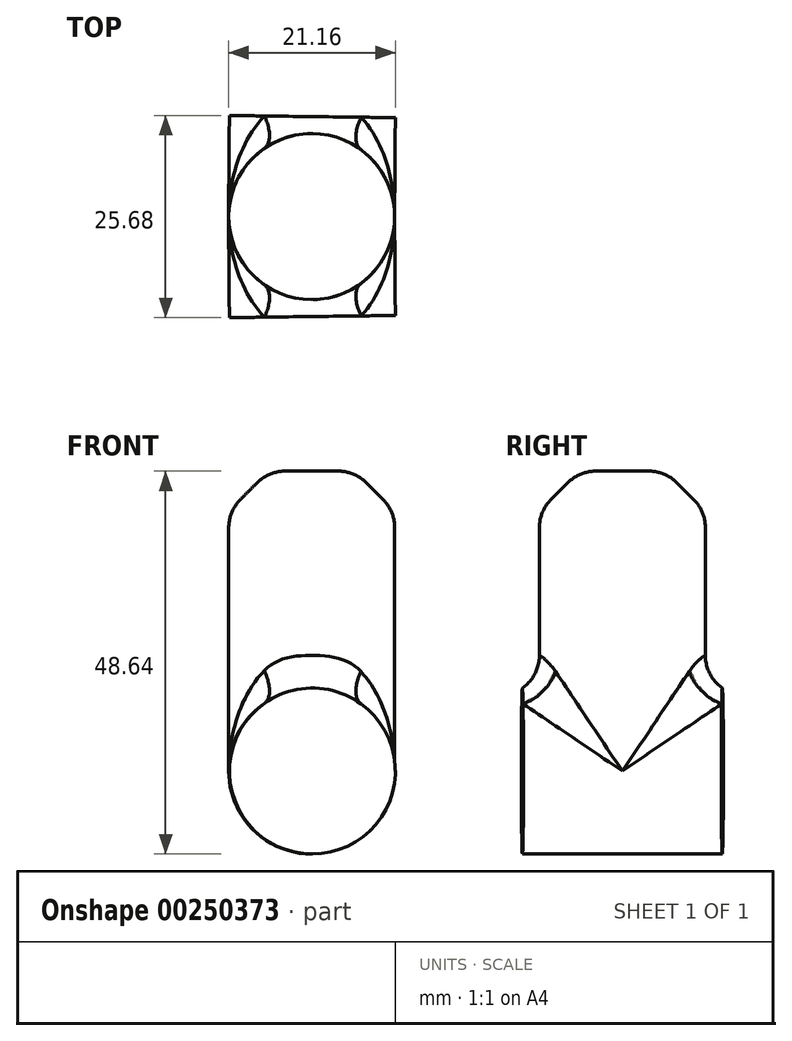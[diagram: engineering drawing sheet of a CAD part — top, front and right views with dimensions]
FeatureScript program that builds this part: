
annotation { "Feature Type Name" : "Feature", "Feature Type Description" : "" }
export const myFeature = defineFeature(function(context is Context, id is Id, definition is map)
    precondition{}
    {
        {
            var Q0;
            Q0=qCreatedBy(makeId("Front.planeOp"),FACE);
            var sketch = newSketch(context, id + "F0", { "sketchPlane" : qUnion([Q0])});
            skCircle(sketch, "E0", {"center": v(0, 0) * mm, "radius": 7.62 * mm});
            skSolve(sketch);
        }
        {
            var Q0;
            Q0=qCreatedBy(makeId("Top.planeOp"),FACE);
            var sketch = newSketch(context, id + "F1", { "sketchPlane" : qUnion([Q0])});
            skCircle(sketch, "E1", {"center": v(977.9, 0) * mm, "radius": 977.9 * mm});
            skSolve(sketch);
        }
        {
            var Q0;
            Q0=makeQuery(id+"F0.imprint","IMPRINT",FACE,{"disambiguationData":[TD([[makeQuery(id+"F0.imprint","IMPRINT",EDGE,{"derivedFrom":sQuery(id+"F0.wireOp",EDGE,"E0")}),1.0]])]});
            var Q1;
            Q1=sQuery(id+"F1.wireOp",EDGE,"E1");
            sweep(context, id + "F2", {"profiles" : qUnion([Q0]), "path" : qUnion([Q1])});
        }
        {
            var Q0;
            Q0=qCreatedBy(makeId("Top.planeOp"),FACE);
            var sketch = newSketch(context, id + "F3", { "sketchPlane" : qUnion([Q0])});
            skLineSegment(sketch, "E2", {"start": v(977.9, 0) * mm, "end": v(-170.26, 44.73) * mm});
            skLineSegment(sketch, "E3", {"start": v(977.9, 0) * mm, "end": v(-241.1, -47.5) * mm});
            skLineSegment(sketch, "E4", {"start": v(-241.1, -47.5) * mm, "end": v(2528.35, -4457.28) * mm});
            skLineSegment(sketch, "E5", {"start": v(2528.35, -4457.28) * mm, "end": v(3546.83, 7722.85) * mm});
            skLineSegment(sketch, "E6", {"start": v(3546.83, 7722.85) * mm, "end": v(-170.26, 44.73) * mm});
            skLineSegment(sketch, "E7", {"start": v(0, 0) * mm, "end": v(0, 38.1) * mm, "construction": true});
            skLineSegment(sketch, "E8", {"start": v(0, 0) * mm, "end": v(0, -38.1) * mm, "construction": true});
            skSolve(sketch);
        }
        {
            var Q0;
            Q0 = qSketchRegion(id + "F3", true);
            extrude(context, id + "F4", {"entities" : qUnion([Q0]), "operationType" : NewBodyOperationType.REMOVE, "endBound" : BoundingType.SYMMETRIC, "depth" : 25.4 * mm});
        }
        {
            var Q0;
            Q0=qCreatedBy(makeId("Front.planeOp"),FACE);
            var sketch = newSketch(context, id + "F5", { "sketchPlane" : qUnion([Q0])});
            skCircle(sketch, "E9", {"center": v(0, 0) * mm, "radius": 10.54 * mm});
            skSolve(sketch);
        }
        {
            var Q0;
            Q0=makeQuery(id+"F5.imprint","IMPRINT",FACE,{"disambiguationData":[TD([[makeQuery(id+"F5.imprint","IMPRINT",EDGE,{"derivedFrom":sQuery(id+"F5.wireOp",EDGE,"E9")}),1.0]])]});
            var Q1;
            Q1=sQuery(id+"F1.wireOp",EDGE,"E1");
            sweep(context, id + "F6", {"profiles" : qUnion([Q0]), "path" : qUnion([Q1])});
        }
        {
            var Q0;
            Q0=qCreatedBy(makeId("Top.planeOp"),FACE);
            var sketch = newSketch(context, id + "F7", { "sketchPlane" : qUnion([Q0])});
            skLineSegment(sketch, "E10", {"start": v(977.9, 0) * mm, "end": v(-988.43, 25.54) * mm});
            skLineSegment(sketch, "E11", {"start": v(977.9, 0) * mm, "end": v(-1458.63, -31.64) * mm});
            skLineSegment(sketch, "E12", {"start": v(-1458.63, -31.64) * mm, "end": v(2080.04, -1798.96) * mm});
            skLineSegment(sketch, "E13", {"start": v(2080.04, -1798.96) * mm, "end": v(2543.06, 2618.35) * mm});
            skLineSegment(sketch, "E14", {"start": v(2543.06, 2618.35) * mm, "end": v(-988.43, 25.54) * mm});
            skLineSegment(sketch, "E15", {"start": v(0, 0) * mm, "end": v(0, 12.7) * mm, "construction": true});
            skLineSegment(sketch, "E16", {"start": v(0, 0) * mm, "end": v(0, -12.7) * mm, "construction": true});
            skSolve(sketch);
        }
        {
            var Q0;
            Q0 = qSketchRegion(id + "F7", true);
            extrude(context, id + "F8", {"entities" : qUnion([Q0]), "operationType" : NewBodyOperationType.REMOVE, "endBound" : BoundingType.SYMMETRIC, "oppositeDirection" : true, "depth" : 25.4 * mm});
        }
        {
            var Q0;
            Q0=qCreatedBy(makeId("Top.planeOp"),FACE);
            var sketch = newSketch(context, id + "F9", { "sketchPlane" : qUnion([Q0])});
            skCircle(sketch, "E17", {"center": v(0, 0) * mm, "radius": 10.54 * mm});
            skSolve(sketch);
        }
        {
            var Q0;
            Q0 = qSketchRegion(id + "F9", true);
            extrude(context, id + "F10", {"entities" : qUnion([Q0]), "operationType" : NewBodyOperationType.ADD, "depth" : 38.1 * mm});
        }
        {
            var Q0;
            Q0=makeQuery(id+"F10.boolean.opBoolean","INTERSECT",EDGE,{"disambiguationData":[OD(0.0)],"derivedFrom":[makeQuery(id+"F6.opSweep","SWEPT_FACE",FACE,{"disambiguationData":[OSD([sQuery(id+"F1.wireOp",EDGE,"E1"),sQuery(id+"F5.wireOp",EDGE,"E9")])]}),makeQuery(id+"F10.opExtrude","SWEPT_FACE",FACE,{"disambiguationData":[OSD([sQuery(id+"F9.wireOp",EDGE,"E17")])]})]});
            var Q1;
            Q1=makeQuery(id+"F10.boolean.opBoolean","INTERSECT",EDGE,{"disambiguationData":[OD(1.0)],"derivedFrom":[makeQuery(id+"F6.opSweep","SWEPT_FACE",FACE,{"disambiguationData":[OSD([sQuery(id+"F1.wireOp",EDGE,"E1"),sQuery(id+"F5.wireOp",EDGE,"E9")])]}),makeQuery(id+"F10.opExtrude","SWEPT_FACE",FACE,{"disambiguationData":[OSD([sQuery(id+"F9.wireOp",EDGE,"E17")])]})]});
            fillet(context, id + "F11", {"entities" : qUnion([Q0, Q1]), "radius" : 5.08 * mm, "tangentPropagation" : true, "allowEdgeOverflow" : false});
        }
        {
            var Q0;
            Q0=makeQuery(id+"F10.opExtrude","CAP_EDGE",EDGE,{"disambiguationData":[OSD([sQuery(id+"F9.wireOp",EDGE,"E17")])],"isStart":false});
            chamfer(context, id + "F12", {"entities" : qUnion([Q0]), "width" : 5.08 * mm, "tangentPropagation" : true});
        }
        {
            var Q0;
            {var subQ0=sQuery(id+"F9.wireOp",EDGE,"E17");Q0=makeQuery(id+"F12.opChamfer","BLEND_EDGE",EDGE,{"blendedFrom":[makeQuery(id+"F10.opExtrude","CAP_EDGE",EDGE,{"disambiguationData":[OSD([subQ0])],"isStart":false}),makeQuery(id+"F10.opExtrude","SWEPT_FACE",FACE,{"disambiguationData":[OSD([subQ0])]})],"blendedInto":[makeQuery(id+"F10.opExtrude","SWEPT_FACE",FACE,{"disambiguationData":[OSD([subQ0])]})]});}
            var Q1;
            {var subQ0=sQuery(id+"F9.wireOp",EDGE,"E17");Q1=makeQuery(id+"F12.opChamfer","BLEND_EDGE",EDGE,{"blendedFrom":[makeQuery(id+"F10.opExtrude","CAP_EDGE",EDGE,{"disambiguationData":[OSD([subQ0])],"isStart":false}),makeQuery(id+"F10.opExtrude","CAP_FACE",FACE,{"disambiguationData":[OSD([subQ0])],"isStart":false})],"blendedInto":[makeQuery(id+"F10.opExtrude","CAP_FACE",FACE,{"disambiguationData":[OSD([subQ0])],"isStart":false})]});}
            fillet(context, id + "F13", {"entities" : qUnion([Q0, Q1]), "radius" : 5.08 * mm, "tangentPropagation" : true, "allowEdgeOverflow" : false});
        }
    });
